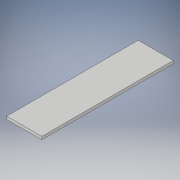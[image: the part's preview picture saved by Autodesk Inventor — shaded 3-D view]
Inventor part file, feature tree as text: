
AUTODESK INVENTOR PART (.ipt)
format: ipt  version: 2019 (Build 230136000, 136)  size: 90,624 bytes
history: native  units: mm
features: other x1, extrude x1, sketch x1
ambient origin geometry x8: Origin, YZ Plane, XZ Plane, XY Plane, X Axis, Y Axis, Z Axis, Center Point
bodies: Body1 (feature_tree)
feature tree (3):
  other  "Těleso1"
  extrude  "Vysunutí1"  Depth=120.0mm
  sketch  "Náčrt1"
